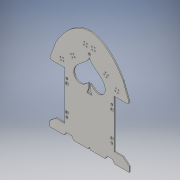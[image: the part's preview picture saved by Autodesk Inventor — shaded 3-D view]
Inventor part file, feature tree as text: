
AUTODESK INVENTOR PART (.ipt)
format: ipt  version: 2016 (Build 200138000, 138)  size: 443,392 bytes
history: native  units: mm
features: other x6, extrude x3, chamfer x1, sketch x1
ambient origin geometry x8: Origin, YZ Plane, XZ Plane, XY Plane, X Axis, Y Axis, Z Axis, Center Point
bodies: Body1 (feature_tree)
feature tree (11):
  other  "shitaita"
  other  "肉抜き"
  other  "作業平面1"
  other  "スペード"
  other  "作業平面3"
  extrude  "押し出し11"  Depth=46.0mm
  extrude  "押し出し12"  Depth=23.5mm
  extrude  "押し出し16"  Depth=23.5mm
  chamfer  "面取り1"  Distance=32.0mm
  sketch  "スケッチ20"
  other  "断面エッジを投影3"
